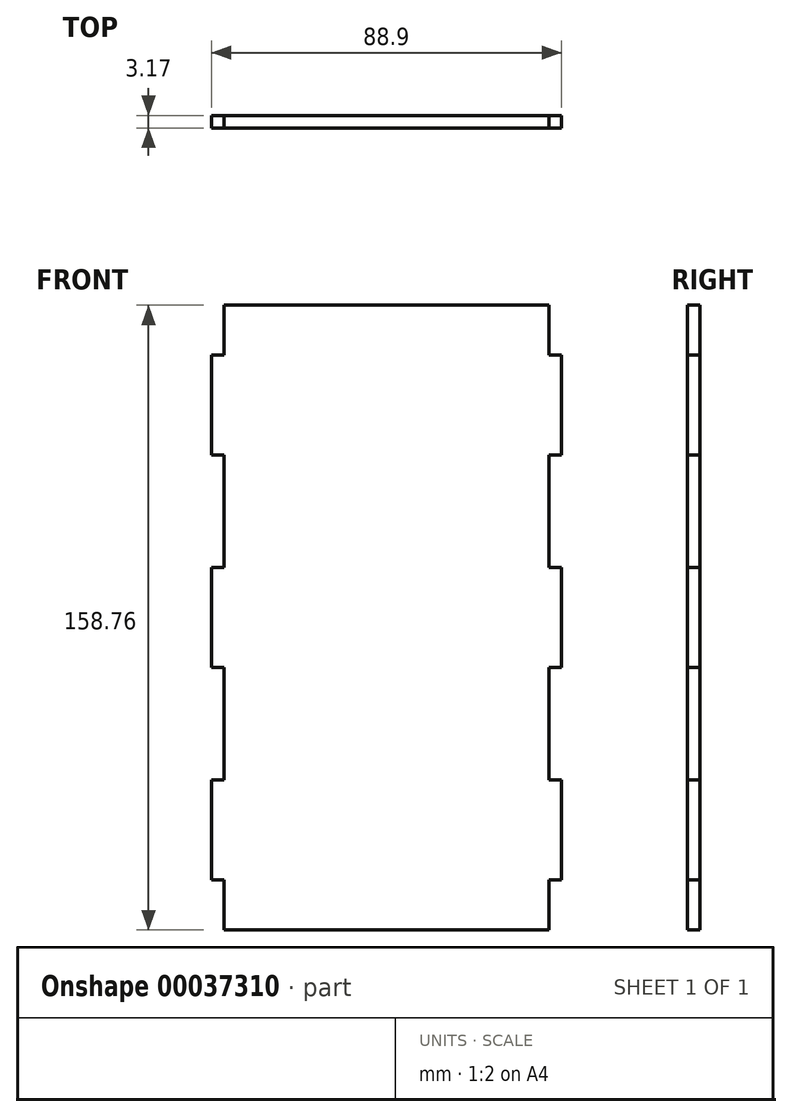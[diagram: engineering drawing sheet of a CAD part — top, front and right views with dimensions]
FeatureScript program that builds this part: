
annotation { "Feature Type Name" : "Feature", "Feature Type Description" : "" }
export const myFeature = defineFeature(function(context is Context, id is Id, definition is map)
    precondition{}
    {
        {
            var Q0;
            Q0=qCreatedBy(makeId("Front.planeOp"),FACE);
            var sketch = newSketch(context, id + "F0", { "sketchPlane" : qUnion([Q0])});
            skLineSegment(sketch, "E0.rect.bottom", {"start": v(44.45, -79.38) * mm, "end": v(-44.45, -79.38) * mm});
            skLineSegment(sketch, "E0.rect.top", {"start": v(44.45, 79.38) * mm, "end": v(-44.45, 79.38) * mm});
            skLineSegment(sketch, "E0.rect.left", {"start": v(44.45, -79.37) * mm, "end": v(44.45, 79.38) * mm});
            skLineSegment(sketch, "E0.rect.right", {"start": v(-44.45, -79.38) * mm, "end": v(-44.45, 79.38) * mm});
            skPoint(sketch, "E0.rect.middle", {"position": v(0, 0) * mm});
            skLineSegment(sketch, "E1", {"start": v(0, 79.38) * mm, "end": v(0, -79.38) * mm, "construction": true});
            skLineSegment(sketch, "E2", {"start": v(-41.28, 79.38) * mm, "end": v(-41.27, -79.38) * mm});
            skLineSegment(sketch, "E3", {"start": v(-41.28, 66.68) * mm, "end": v(-44.45, 66.68) * mm});
            skLineSegment(sketch, "E4", {"start": v(-44.45, -66.68) * mm, "end": v(-41.27, -66.68) * mm});
            skLineSegment(sketch, "E5", {"start": v(-44.45, 41.27) * mm, "end": v(-41.28, 41.27) * mm});
            skLineSegment(sketch, "E6", {"start": v(-41.28, 12.7) * mm, "end": v(-44.45, 12.7) * mm});
            skLineSegment(sketch, "E7", {"start": v(-44.45, -12.7) * mm, "end": v(-41.27, -12.7) * mm});
            skLineSegment(sketch, "E8", {"start": v(-41.27, -41.28) * mm, "end": v(-44.45, -41.28) * mm});
            skLineSegment(sketch, "E9.MirrorCS", {"start": v(41.27, 66.68) * mm, "end": v(44.45, 66.68) * mm});
            skLineSegment(sketch, "E10.MirrorCS", {"start": v(41.27, 79.38) * mm, "end": v(41.28, -79.37) * mm});
            skLineSegment(sketch, "E11.MirrorCS", {"start": v(44.45, 41.27) * mm, "end": v(41.28, 41.27) * mm});
            skLineSegment(sketch, "E12.MirrorCS", {"start": v(41.28, 12.7) * mm, "end": v(44.45, 12.7) * mm});
            skLineSegment(sketch, "E13.MirrorCS", {"start": v(44.45, -12.7) * mm, "end": v(41.28, -12.7) * mm});
            skLineSegment(sketch, "E14.MirrorCS", {"start": v(41.28, -41.28) * mm, "end": v(44.45, -41.28) * mm});
            skLineSegment(sketch, "E15.MirrorCS", {"start": v(44.45, -66.67) * mm, "end": v(41.28, -66.67) * mm});
            skSolve(sketch);
        }
        {
            var Q0;
            {var subQ9=sQuery(id+"F0.wireOp",EDGE,"E2");var subQ11=sQuery(id+"F0.wireOp",EDGE,"E0.rect.bottom");var subQ12=makeQuery(id+"F0.imprint","INTERSECT",VERTEX,{"derivedFrom":[subQ11,subQ9]});Q0=makeQuery(id+"F0.imprint","IMPRINT",FACE,{"disambiguationData":[TD([[makeQuery(id+"F0.imprint","IMPRINT",EDGE,{"disambiguationData":[TD([[subQ12,1.0]])],"derivedFrom":subQ11}),-1.0]])]});}
            var Q1;
            {var subQ2=sQuery(id+"F0.wireOp",EDGE,"E3");Q1=makeQuery(id+"F0.imprint","IMPRINT",FACE,{"disambiguationData":[TD([[makeQuery(id+"F0.imprint","IMPRINT",EDGE,{"derivedFrom":subQ2}),1.0]])]});}
            var Q2;
            {var subQ1=sQuery(id+"F0.wireOp",EDGE,"E6");Q2=makeQuery(id+"F0.imprint","IMPRINT",FACE,{"disambiguationData":[TD([[makeQuery(id+"F0.imprint","IMPRINT",EDGE,{"derivedFrom":subQ1}),1.0]])]});}
            var Q3;
            {var subQ0=sQuery(id+"F0.wireOp",EDGE,"E4");Q3=makeQuery(id+"F0.imprint","IMPRINT",FACE,{"disambiguationData":[TD([[makeQuery(id+"F0.imprint","IMPRINT",EDGE,{"derivedFrom":subQ0}),1.0]])]});}
            var Q4;
            {var subQ1=sQuery(id+"F0.wireOp",EDGE,"E14.MirrorCS");Q4=makeQuery(id+"F0.imprint","IMPRINT",FACE,{"disambiguationData":[TD([[makeQuery(id+"F0.imprint","IMPRINT",EDGE,{"derivedFrom":subQ1}),-1.0]])]});}
            var Q5;
            {var subQ1=sQuery(id+"F0.wireOp",EDGE,"E12.MirrorCS");Q5=makeQuery(id+"F0.imprint","IMPRINT",FACE,{"disambiguationData":[TD([[makeQuery(id+"F0.imprint","IMPRINT",EDGE,{"derivedFrom":subQ1}),-1.0]])]});}
            var Q6;
            {var subQ2=sQuery(id+"F0.wireOp",EDGE,"E9.MirrorCS");Q6=makeQuery(id+"F0.imprint","IMPRINT",FACE,{"disambiguationData":[TD([[makeQuery(id+"F0.imprint","IMPRINT",EDGE,{"derivedFrom":subQ2}),-1.0]])]});}
            extrude(context, id + "F1", {"entities" : qUnion([Q0, Q1, Q2, Q3, Q4, Q5, Q6]), "depth" : 3.17 * mm});
        }
    });
